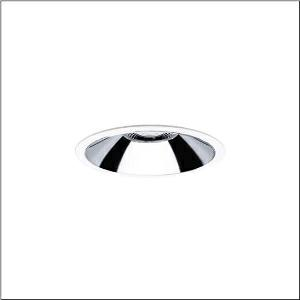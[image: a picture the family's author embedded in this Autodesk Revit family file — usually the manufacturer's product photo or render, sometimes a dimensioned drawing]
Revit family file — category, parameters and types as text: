
# Revit family: lunis_21_xl_51db15mf4d
name_source: partatom
category: Lighting Fixtures
units: mm (PartAtom-declared; Revit-internal decimal feet)

## family parameters
Cut with Voids When Loaded = No
Host = Face
Light Source = No
Part Type = Normal
Room Calculation Point = No
Round Connector Dimension = Use Diameter
Shared = No

## types (1)
- --- (1 x LED, 3000 lm, 24.3 W, 4000K)
    Apparent Load = 24 VA
    CIE Flux Codes = 89 99 100 100 100
    Color Rendering = 80
    Color Temperature = 4000K
    Default Elevation = 1800 mm
    Description = Lunis 21,  XL, downlight, of PC, light emission: direct distribution, LED rated luminous flux: 2.280lm, light colour: 840, control gear: ECG, with terminal, 3-pole, mains connection: 220..240V, AC, housing, round, of diecast aluminium, traffic white (RAL 9016), diameter: 213mm, protection rating (complete): IP20, protection rating (on room side): IP54, insulation class (complete): insulation class II (safety insulation), certification: CE, impact resistance: IK02, packaging unit: 1 piece
    Height = 0 mm  [stored 0 ft]
    Lamp = 1 x LED
    Lamp Light Flux = 3000 lm
    Lamp Power = 24.3 W
    Lamp count = 1
    Length = 213 mm
    Luminous efficacy = 123 lm/W
    Manufacturer = Siteco
    ModVariant = No
    Model = 51DB15MF4D
    Mounting Place = Ceiling
    Mounting Type = Recessed
    Number of Poles = 1
    OnlyDefault = Yes
    Power Factor = 1
    Product Name = Lunis 21 XL
    Product group = downlight
    ProductGroupID = 400
    Protection Class = Protection class II
    Protection Degree = IP 20
    RLX_Detail_Level = 1
    RLX_Emergency_Light_Flux = 0 lm
    RLX_Emergency_Type = 0
    RLX_Emergency_Type_DB = No
    RlxData = <blob elided: 27589 chars, md5=87faddd5>
    Socket = socket
    Standby Power = 0 W
    System Light Flux = 3000 lm
    System Power = 24 W
    Type Comments = factory setting: luminous flux: 100 % | (ON | ON)
    Type Image = l_1287385.jpg
    URL = http://relux.com
    VarID = @adj_083067
    Voltage = 0 V
    Weight = 0.00 kg
    Width = 0 mm  [stored 0 ft]

note: [stored X ft] marks values corroborated as IEEE doubles in the binary element streams (Revit-internal decimal feet)

## geometry (parser evidence)
native form markers: Blend x4, Sweep x12
no freeform markers — native parametric forms only
